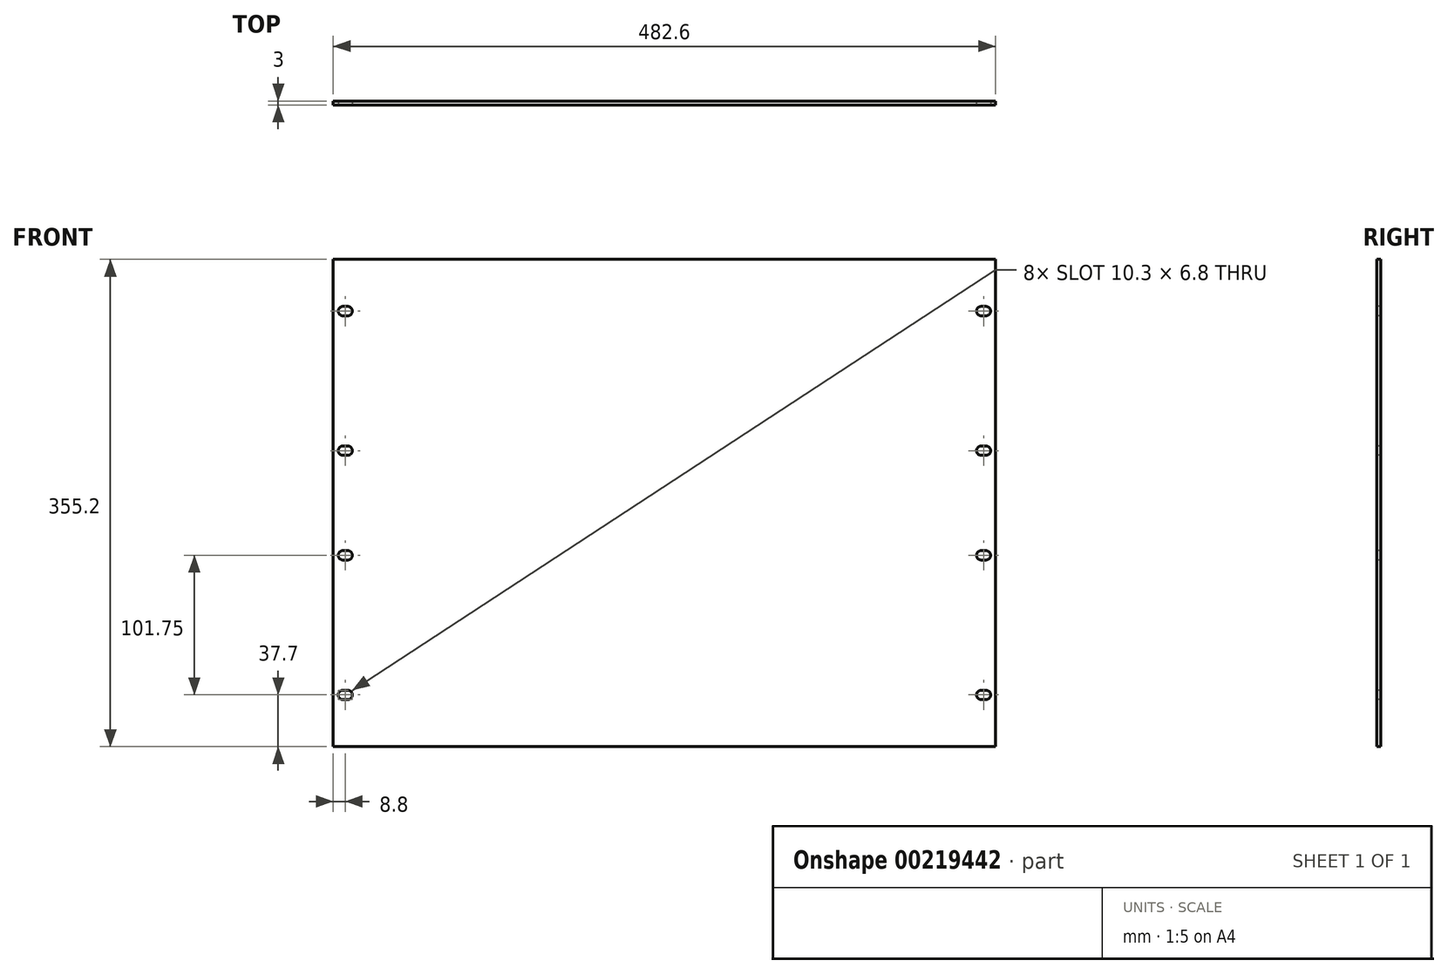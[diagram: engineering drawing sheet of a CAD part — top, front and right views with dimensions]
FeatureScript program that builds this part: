
annotation { "Feature Type Name" : "Feature", "Feature Type Description" : "" }
export const myFeature = defineFeature(function(context is Context, id is Id, definition is map)
    precondition{}
    {
        {
            var Q0;
            Q0=qCreatedBy(makeId("Front.planeOp"),FACE);
            var sketch = newSketch(context, id + "F0", { "sketchPlane" : qUnion([Q0])});
            skLineSegment(sketch, "E0.bottom", {"start": v(-241.3, 177.6) * mm, "end": v(241.3, 177.6) * mm});
            skLineSegment(sketch, "E0.top", {"start": v(-241.3, -177.6) * mm, "end": v(241.3, -177.6) * mm});
            skLineSegment(sketch, "E0.left", {"start": v(-241.3, 177.6) * mm, "end": v(-241.3, -177.6) * mm});
            skLineSegment(sketch, "E0.right", {"start": v(241.3, 177.6) * mm, "end": v(241.3, -177.6) * mm});
            skPoint(sketch, "E0.middle", {"position": v(0, 0) * mm});
            skSolve(sketch);
        }
        {
            var Q0;
            Q0=qSketchRegion(id+"F0",true);
            extrude(context, id + "F1", {"entities" : qUnion([Q0]), "oppositeDirection" : true, "depth" : 3 * mm});
        }
        {
            var Q0;
            Q0=makeQuery(id+"F1.opExtrude","CAP_FACE",FACE,{"disambiguationData":[OSD([sQuery(id+"F0.wireOp",EDGE,"E0.bottom"),sQuery(id+"F0.wireOp",EDGE,"E0.top"),sQuery(id+"F0.wireOp",EDGE,"E0.left"),sQuery(id+"F0.wireOp",EDGE,"E0.right")])],"isStart":true});
            var sketch = newSketch(context, id + "F2", { "sketchPlane" : qUnion([Q0])});
            skLineSegment(sketch, "E1.bottom", {"start": v(-230.75, 136.5) * mm, "end": v(-234.25, 136.5) * mm});
            skLineSegment(sketch, "E1.top", {"start": v(-230.75, 143.3) * mm, "end": v(-234.25, 143.3) * mm});
            skLineSegment(sketch, "E1.left", {"start": v(-230.75, 136.5) * mm, "end": v(-230.75, 143.3) * mm});
            skLineSegment(sketch, "E1.right", {"start": v(-234.25, 136.5) * mm, "end": v(-234.25, 143.3) * mm});
            skPoint(sketch, "E1.middle", {"position": v(-232.5, 139.9) * mm});
            skArc(sketch, "E2", {"start": v(-230.75, 136.5) * mm, "mid": v(-227.35, 139.9) * mm, "end": v(-230.75, 143.3) * mm});
            skArc(sketch, "E3", {"start": v(-234.25, 143.3) * mm, "mid": v(-237.65, 139.9) * mm, "end": v(-234.25, 136.5) * mm});
            skSolve(sketch);
        }
        {
            var Q0;
            Q0=makeQuery(id+"F2.imprint","IMPRINT",FACE,{"disambiguationData":[TD([[makeQuery(id+"F2.imprint","IMPRINT",EDGE,{"derivedFrom":sQuery(id+"F2.wireOp",EDGE,"E1.bottom")}),1.0]])]});
            var sketch = newSketch(context, id + "F3", { "sketchPlane" : qUnion([Q0])});
            skLineSegment(sketch, "E4.bottom", {"start": v(-230.75, 34.75) * mm, "end": v(-234.25, 34.75) * mm});
            skLineSegment(sketch, "E4.top", {"start": v(-230.75, 41.55) * mm, "end": v(-234.25, 41.55) * mm});
            skLineSegment(sketch, "E4.left", {"start": v(-230.75, 34.75) * mm, "end": v(-230.75, 41.55) * mm});
            skLineSegment(sketch, "E4.right", {"start": v(-234.25, 34.75) * mm, "end": v(-234.25, 41.55) * mm});
            skPoint(sketch, "E4.middle", {"position": v(-232.5, 38.15) * mm});
            skArc(sketch, "E5", {"start": v(-230.75, 34.75) * mm, "mid": v(-227.35, 38.15) * mm, "end": v(-230.75, 41.55) * mm});
            skArc(sketch, "E6", {"start": v(-234.25, 41.55) * mm, "mid": v(-237.65, 38.15) * mm, "end": v(-234.25, 34.75) * mm});
            skSolve(sketch);
        }
        {
            var Q0;
            Q0=makeQuery(id+"F2.imprint","IMPRINT",FACE,{"disambiguationData":[TD([[makeQuery(id+"F2.imprint","IMPRINT",EDGE,{"derivedFrom":sQuery(id+"F2.wireOp",EDGE,"E1.bottom")}),1.0]])]});
            var sketch = newSketch(context, id + "F4", { "sketchPlane" : qUnion([Q0])});
            skLineSegment(sketch, "E7.bottom", {"start": v(-230.75, -41.55) * mm, "end": v(-234.25, -41.55) * mm});
            skLineSegment(sketch, "E7.top", {"start": v(-230.75, -34.75) * mm, "end": v(-234.25, -34.75) * mm});
            skLineSegment(sketch, "E7.left", {"start": v(-230.75, -41.55) * mm, "end": v(-230.75, -34.75) * mm});
            skLineSegment(sketch, "E7.right", {"start": v(-234.25, -41.55) * mm, "end": v(-234.25, -34.75) * mm});
            skPoint(sketch, "E7.middle", {"position": v(-232.5, -38.15) * mm});
            skArc(sketch, "E8", {"start": v(-230.75, -41.55) * mm, "mid": v(-227.35, -38.15) * mm, "end": v(-230.75, -34.75) * mm});
            skArc(sketch, "E9", {"start": v(-234.25, -34.75) * mm, "mid": v(-237.65, -38.15) * mm, "end": v(-234.25, -41.55) * mm});
            skSolve(sketch);
        }
        {
            var Q0;
            Q0=makeQuery(id+"F2.imprint","IMPRINT",FACE,{"disambiguationData":[TD([[makeQuery(id+"F2.imprint","IMPRINT",EDGE,{"derivedFrom":sQuery(id+"F2.wireOp",EDGE,"E1.bottom")}),1.0]])]});
            var sketch = newSketch(context, id + "F5", { "sketchPlane" : qUnion([Q0])});
            skLineSegment(sketch, "E10.bottom", {"start": v(-234.25, -136.5) * mm, "end": v(-230.75, -136.5) * mm});
            skLineSegment(sketch, "E10.top", {"start": v(-234.25, -143.3) * mm, "end": v(-230.75, -143.3) * mm});
            skLineSegment(sketch, "E10.left", {"start": v(-234.25, -136.5) * mm, "end": v(-234.25, -143.3) * mm});
            skLineSegment(sketch, "E10.right", {"start": v(-230.75, -136.5) * mm, "end": v(-230.75, -143.3) * mm});
            skPoint(sketch, "E10.middle", {"position": v(-232.5, -139.9) * mm});
            skArc(sketch, "E11", {"start": v(-230.75, -143.3) * mm, "mid": v(-227.35, -139.9) * mm, "end": v(-230.75, -136.5) * mm});
            skArc(sketch, "E12", {"start": v(-234.25, -136.5) * mm, "mid": v(-237.65, -139.9) * mm, "end": v(-234.25, -143.3) * mm});
            skSolve(sketch);
        }
        {
            var Q0;
            Q0=qSketchRegion(id+"F2",true);
            var Q1;
            Q1=qSketchRegion(id+"F3",true);
            var Q2;
            Q2=qSketchRegion(id+"F4",true);
            var Q3;
            Q3=qSketchRegion(id+"F5",true);
            extrude(context, id + "F6", {"entities" : qUnion([Q0, Q1, Q2, Q3]), "operationType" : NewBodyOperationType.REMOVE, "oppositeDirection" : true, "depth" : 3 * mm});
        }
        {
            var Q0;
            Q0=makeQuery(id+"F1.opExtrude","CAP_FACE",FACE,{"disambiguationData":[OSD([sQuery(id+"F0.wireOp",EDGE,"E0.bottom"),sQuery(id+"F0.wireOp",EDGE,"E0.top"),sQuery(id+"F0.wireOp",EDGE,"E0.left"),sQuery(id+"F0.wireOp",EDGE,"E0.right")])],"isStart":true});
            var sketch = newSketch(context, id + "F7", { "sketchPlane" : qUnion([Q0])});
            skLineSegment(sketch, "E13.bottom", {"start": v(234.25, 136.5) * mm, "end": v(230.75, 136.5) * mm});
            skLineSegment(sketch, "E13.top", {"start": v(234.25, 143.3) * mm, "end": v(230.75, 143.3) * mm});
            skLineSegment(sketch, "E13.left", {"start": v(234.25, 136.5) * mm, "end": v(234.25, 143.3) * mm});
            skLineSegment(sketch, "E13.right", {"start": v(230.75, 136.5) * mm, "end": v(230.75, 143.3) * mm});
            skPoint(sketch, "E13.middle", {"position": v(232.5, 139.9) * mm});
            skArc(sketch, "E14", {"start": v(230.75, 143.3) * mm, "mid": v(227.35, 139.9) * mm, "end": v(230.75, 136.5) * mm});
            skArc(sketch, "E15", {"start": v(234.25, 136.5) * mm, "mid": v(237.65, 139.9) * mm, "end": v(234.25, 143.3) * mm});
            skSolve(sketch);
        }
        {
            var Q0;
            Q0=makeQuery(id+"F7.imprint","IMPRINT",FACE,{"disambiguationData":[TD([[makeQuery(id+"F7.imprint","IMPRINT",EDGE,{"derivedFrom":sQuery(id+"F7.wireOp",EDGE,"E13.bottom")}),1.0]])]});
            var sketch = newSketch(context, id + "F8", { "sketchPlane" : qUnion([Q0])});
            skLineSegment(sketch, "E16.bottom", {"start": v(234.25, 34.75) * mm, "end": v(230.75, 34.75) * mm});
            skLineSegment(sketch, "E16.top", {"start": v(234.25, 41.55) * mm, "end": v(230.75, 41.55) * mm});
            skLineSegment(sketch, "E16.left", {"start": v(234.25, 34.75) * mm, "end": v(234.25, 41.55) * mm});
            skLineSegment(sketch, "E16.right", {"start": v(230.75, 34.75) * mm, "end": v(230.75, 41.55) * mm});
            skPoint(sketch, "E16.middle", {"position": v(232.5, 38.15) * mm});
            skArc(sketch, "E17", {"start": v(234.25, 34.75) * mm, "mid": v(237.65, 38.15) * mm, "end": v(234.25, 41.55) * mm});
            skArc(sketch, "E18", {"start": v(230.75, 41.55) * mm, "mid": v(227.35, 38.15) * mm, "end": v(230.75, 34.75) * mm});
            skSolve(sketch);
        }
        {
            var Q0;
            Q0=makeQuery(id+"F7.imprint","IMPRINT",FACE,{"disambiguationData":[TD([[makeQuery(id+"F7.imprint","IMPRINT",EDGE,{"derivedFrom":sQuery(id+"F7.wireOp",EDGE,"E13.bottom")}),1.0]])]});
            var sketch = newSketch(context, id + "F9", { "sketchPlane" : qUnion([Q0])});
            skLineSegment(sketch, "E19.bottom", {"start": v(234.25, -41.55) * mm, "end": v(230.75, -41.55) * mm});
            skLineSegment(sketch, "E19.top", {"start": v(234.25, -34.75) * mm, "end": v(230.75, -34.75) * mm});
            skLineSegment(sketch, "E19.left", {"start": v(234.25, -41.55) * mm, "end": v(234.25, -34.75) * mm});
            skLineSegment(sketch, "E19.right", {"start": v(230.75, -41.55) * mm, "end": v(230.75, -34.75) * mm});
            skPoint(sketch, "E19.middle", {"position": v(232.5, -38.15) * mm});
            skArc(sketch, "E20", {"start": v(234.25, -41.55) * mm, "mid": v(237.65, -38.15) * mm, "end": v(234.25, -34.75) * mm});
            skArc(sketch, "E21", {"start": v(230.75, -34.75) * mm, "mid": v(227.35, -38.15) * mm, "end": v(230.75, -41.55) * mm});
            skSolve(sketch);
        }
        {
            var Q0;
            Q0=makeQuery(id+"F7.imprint","IMPRINT",FACE,{"disambiguationData":[TD([[makeQuery(id+"F7.imprint","IMPRINT",EDGE,{"derivedFrom":sQuery(id+"F7.wireOp",EDGE,"E13.bottom")}),1.0]])]});
            var sketch = newSketch(context, id + "F10", { "sketchPlane" : qUnion([Q0])});
            skLineSegment(sketch, "E22.bottom", {"start": v(234.25, -143.3) * mm, "end": v(230.75, -143.3) * mm});
            skLineSegment(sketch, "E22.top", {"start": v(234.25, -136.5) * mm, "end": v(230.75, -136.5) * mm});
            skLineSegment(sketch, "E22.left", {"start": v(234.25, -143.3) * mm, "end": v(234.25, -136.5) * mm});
            skLineSegment(sketch, "E22.right", {"start": v(230.75, -143.3) * mm, "end": v(230.75, -136.5) * mm});
            skPoint(sketch, "E22.middle", {"position": v(232.5, -139.9) * mm});
            skArc(sketch, "E23", {"start": v(234.25, -143.3) * mm, "mid": v(237.65, -139.9) * mm, "end": v(234.25, -136.5) * mm});
            skArc(sketch, "E24", {"start": v(230.75, -136.5) * mm, "mid": v(227.35, -139.9) * mm, "end": v(230.75, -143.3) * mm});
            skSolve(sketch);
        }
        {
            var Q0;
            Q0=qSketchRegion(id+"F7",true);
            var Q1;
            Q1=qSketchRegion(id+"F8",true);
            var Q2;
            Q2=qSketchRegion(id+"F9",true);
            var Q3;
            Q3=qSketchRegion(id+"F10",true);
            extrude(context, id + "F11", {"entities" : qUnion([Q0, Q1, Q2, Q3]), "operationType" : NewBodyOperationType.REMOVE, "oppositeDirection" : true, "depth" : 3 * mm});
        }
    });
